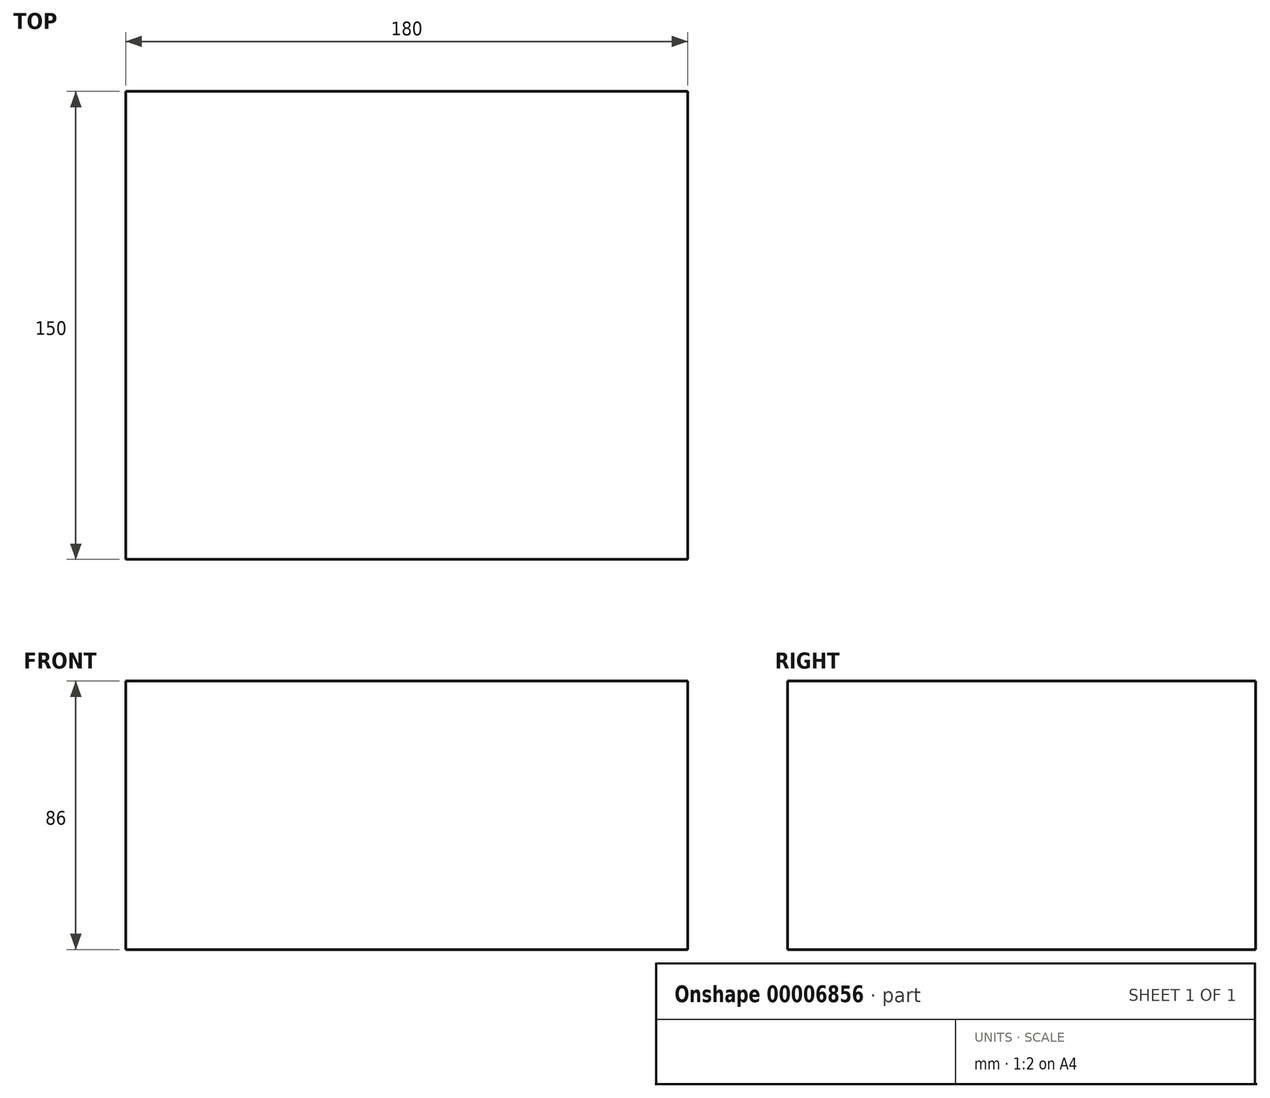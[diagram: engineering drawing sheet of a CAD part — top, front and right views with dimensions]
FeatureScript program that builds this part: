
annotation { "Feature Type Name" : "Feature", "Feature Type Description" : "" }
export const myFeature = defineFeature(function(context is Context, id is Id, definition is map)
    precondition{}
    {
        {
            var Q0;
            Q0=qCreatedBy(makeId("Top.planeOp"),FACE);
            var sketch = newSketch(context, id + "F0", { "sketchPlane" : qUnion([Q0])});
            skLineSegment(sketch, "E0.bottom", {"start": v(-108.59, -48.7) * mm, "end": v(71.41, -48.7) * mm});
            skLineSegment(sketch, "E0.top", {"start": v(-108.59, 101.3) * mm, "end": v(71.41, 101.3) * mm});
            skLineSegment(sketch, "E0.left", {"start": v(-108.59, -48.7) * mm, "end": v(-108.59, 101.3) * mm});
            skLineSegment(sketch, "E0.right", {"start": v(71.41, -48.7) * mm, "end": v(71.41, 101.3) * mm});
            skSolve(sketch);
        }
        {
            var Q0;
            Q0 = qSketchRegion(id + "F0", true);
            extrude(context, id + "F1", {"entities" : qUnion([Q0]), "depth" : 86 * mm});
        }
    });
